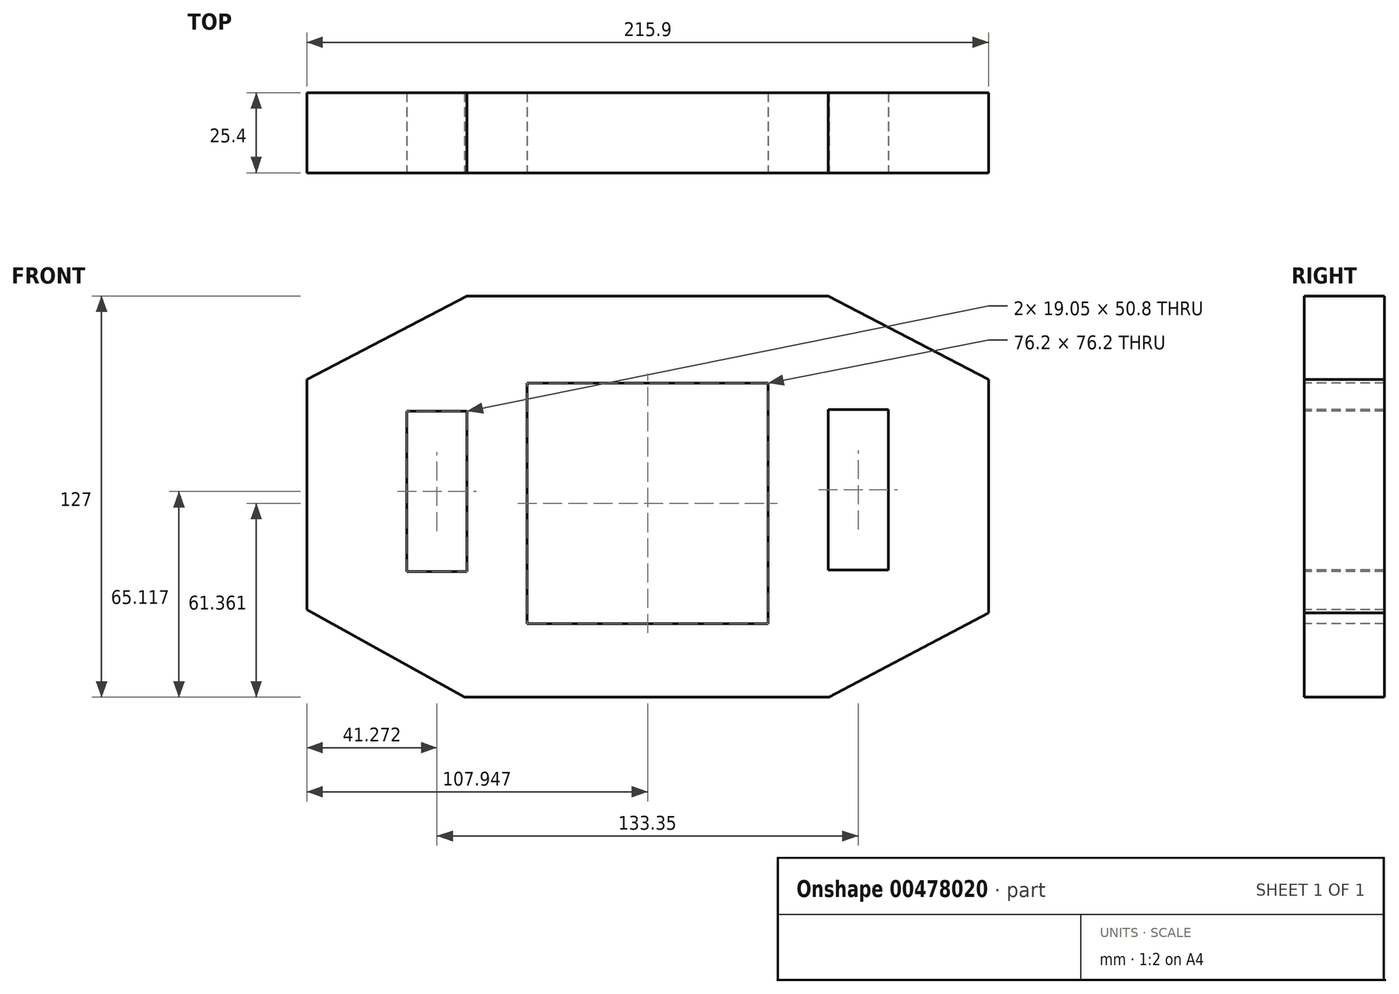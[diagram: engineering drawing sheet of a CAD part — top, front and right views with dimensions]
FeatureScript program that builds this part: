
annotation { "Feature Type Name" : "Feature", "Feature Type Description" : "" }
export const myFeature = defineFeature(function(context is Context, id is Id, definition is map)
    precondition{}
    {
        {
            var Q0;
            Q0=qCreatedBy(makeId("Front.planeOp"),FACE);
            var sketch = newSketch(context, id + "F0", { "sketchPlane" : qUnion([Q0])});
            skLineSegment(sketch, "E0.bottom", {"start": v(-95.14, 58.2) * mm, "end": v(120.76, 58.2) * mm});
            skLineSegment(sketch, "E0.top", {"start": v(-95.14, -68.8) * mm, "end": v(120.76, -68.8) * mm});
            skLineSegment(sketch, "E0.left", {"start": v(-95.14, 58.2) * mm, "end": v(-95.14, -68.8) * mm});
            skLineSegment(sketch, "E0.right", {"start": v(120.76, 58.2) * mm, "end": v(120.76, -68.8) * mm});
            skSolve(sketch);
        }
        {
            var Q0;
            Q0 = qSketchRegion(id + "F0", true);
            extrude(context, id + "F1", {"entities" : qUnion([Q0]), "depth" : 25.4 * mm});
        }
        {
            var Q0;
            Q0=makeQuery(id+"F1.opExtrude","CAP_FACE",FACE,{"disambiguationData":[OSD([sQuery(id+"F0.wireOp",EDGE,"E0.bottom"),sQuery(id+"F0.wireOp",EDGE,"E0.top"),sQuery(id+"F0.wireOp",EDGE,"E0.left"),sQuery(id+"F0.wireOp",EDGE,"E0.right")])],"isStart":false});
            var sketch = newSketch(context, id + "F2", { "sketchPlane" : qUnion([Q0])});
            skLineSegment(sketch, "E1", {"start": v(-95.14, 31.78) * mm, "end": v(-44.46, 58.2) * mm});
            skLineSegment(sketch, "E2", {"start": v(70.07, 58.2) * mm, "end": v(120.76, 31.78) * mm});
            skLineSegment(sketch, "E3", {"start": v(-95.14, -41.18) * mm, "end": v(-45.11, -68.8) * mm});
            skLineSegment(sketch, "E4", {"start": v(70.23, -68.8) * mm, "end": v(120.76, -42.1) * mm});
            skSolve(sketch);
        }
        {
            var Q0;
            {var subQ0=sQuery(id+"F2.wireOp",EDGE,"E1");Q0=makeQuery(id+"F2.imprint","IMPRINT",FACE,{"disambiguationData":[TD([[makeQuery(id+"F2.imprint","IMPRINT",EDGE,{"derivedFrom":subQ0}),1.0]])]});}
            extrude(context, id + "F3", {"entities" : qUnion([Q0]), "operationType" : NewBodyOperationType.REMOVE, "oppositeDirection" : true, "depth" : 25.4 * mm});
        }
        {
            var Q0;
            {var subQ0=sQuery(id+"F2.wireOp",EDGE,"E3");Q0=makeQuery(id+"F2.imprint","IMPRINT",FACE,{"disambiguationData":[TD([[makeQuery(id+"F2.imprint","IMPRINT",EDGE,{"derivedFrom":subQ0}),-1.0]])]});}
            extrude(context, id + "F4", {"entities" : qUnion([Q0]), "operationType" : NewBodyOperationType.REMOVE, "oppositeDirection" : true, "depth" : 25.4 * mm});
        }
        {
            var Q0;
            {var subQ0=sQuery(id+"F2.wireOp",EDGE,"E4");Q0=makeQuery(id+"F2.imprint","IMPRINT",FACE,{"disambiguationData":[TD([[makeQuery(id+"F2.imprint","IMPRINT",EDGE,{"derivedFrom":subQ0}),-1.0]])]});}
            extrude(context, id + "F5", {"entities" : qUnion([Q0]), "operationType" : NewBodyOperationType.REMOVE, "oppositeDirection" : true, "depth" : 25.4 * mm});
        }
        {
            var Q0;
            {var subQ0=sQuery(id+"F2.wireOp",EDGE,"E2");Q0=makeQuery(id+"F2.imprint","IMPRINT",FACE,{"disambiguationData":[TD([[makeQuery(id+"F2.imprint","IMPRINT",EDGE,{"derivedFrom":subQ0}),1.0]])]});}
            extrude(context, id + "F6", {"entities" : qUnion([Q0]), "operationType" : NewBodyOperationType.REMOVE, "oppositeDirection" : true, "depth" : 25.4 * mm});
        }
        {
            var Q0;
            Q0=makeQuery(id+"F1.opExtrude","CAP_FACE",FACE,{"disambiguationData":[OSD([sQuery(id+"F0.wireOp",EDGE,"E0.bottom"),sQuery(id+"F0.wireOp",EDGE,"E0.top"),sQuery(id+"F0.wireOp",EDGE,"E0.left"),sQuery(id+"F0.wireOp",EDGE,"E0.right")])],"isStart":false});
            var sketch = newSketch(context, id + "F7", { "sketchPlane" : qUnion([Q0])});
            skLineSegment(sketch, "E5.bottom", {"start": v(-25.3, 30.65) * mm, "end": v(50.9, 30.65) * mm});
            skLineSegment(sketch, "E5.top", {"start": v(-25.3, -45.55) * mm, "end": v(50.9, -45.55) * mm});
            skLineSegment(sketch, "E5.left", {"start": v(-25.3, 30.65) * mm, "end": v(-25.3, -45.55) * mm});
            skLineSegment(sketch, "E5.right", {"start": v(50.9, 30.65) * mm, "end": v(50.9, -45.55) * mm});
            skSolve(sketch);
        }
        {
            var Q0;
            Q0=makeQuery(id+"F7.imprint","IMPRINT",FACE,{"disambiguationData":[TD([[makeQuery(id+"F7.imprint","IMPRINT",EDGE,{"derivedFrom":sQuery(id+"F7.wireOp",EDGE,"E5.bottom")}),-1.0]])]});
            extrude(context, id + "F8", {"entities" : qUnion([Q0]), "operationType" : NewBodyOperationType.REMOVE, "oppositeDirection" : true, "depth" : 25.4 * mm});
        }
        {
            var Q0;
            Q0=makeQuery(id+"F1.opExtrude","CAP_FACE",FACE,{"disambiguationData":[OSD([sQuery(id+"F0.wireOp",EDGE,"E0.bottom"),sQuery(id+"F0.wireOp",EDGE,"E0.top"),sQuery(id+"F0.wireOp",EDGE,"E0.left"),sQuery(id+"F0.wireOp",EDGE,"E0.right")])],"isStart":false});
            var sketch = newSketch(context, id + "F9", { "sketchPlane" : qUnion([Q0])});
            skLineSegment(sketch, "E6.bottom", {"start": v(-63.4, 21.7) * mm, "end": v(-44.34, 21.7) * mm});
            skLineSegment(sketch, "E6.top", {"start": v(-63.4, -29.1) * mm, "end": v(-44.34, -29.1) * mm});
            skLineSegment(sketch, "E6.left", {"start": v(-63.4, 21.7) * mm, "end": v(-63.4, -29.1) * mm});
            skLineSegment(sketch, "E6.right", {"start": v(-44.34, 21.7) * mm, "end": v(-44.34, -29.1) * mm});
            skLineSegment(sketch, "E7.bottom", {"start": v(69.96, 22.2) * mm, "end": v(89, 22.2) * mm});
            skLineSegment(sketch, "E7.top", {"start": v(69.96, -28.6) * mm, "end": v(89, -28.6) * mm});
            skLineSegment(sketch, "E7.left", {"start": v(69.96, 22.2) * mm, "end": v(69.96, -28.6) * mm});
            skLineSegment(sketch, "E7.right", {"start": v(89, 22.2) * mm, "end": v(89, -28.6) * mm});
            skSolve(sketch);
        }
        {
            var Q0;
            Q0 = qSketchRegion(id + "F9", true);
            extrude(context, id + "F10", {"entities" : qUnion([Q0]), "operationType" : NewBodyOperationType.REMOVE, "oppositeDirection" : true, "depth" : 25.4 * mm});
        }
    });
